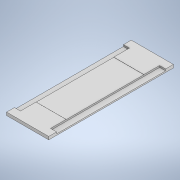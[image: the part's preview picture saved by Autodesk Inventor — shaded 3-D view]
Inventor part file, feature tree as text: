
AUTODESK INVENTOR PART (.ipt)
format: ipt  version: 2020.1 (Build 241239000, 239)  size: 159,744 bytes
history: native  units: mm
features: sketch x6, extrude x5, other x1
ambient origin geometry x8: Origin, YZ Plane, XZ Plane, XY Plane, X Axis, Y Axis, Z Axis, Center Point
bodies: Body1 (feature_tree)
feature tree (12):
  other  "Твердое тело1"
  extrude  "Выдавливание1"  Depth=776.0mm
  extrude  "Выдавливание2"  Depth=280.0mm
  sketch  "Эскиз4"
  extrude  "Выдавливание3"  Depth=20.0mm TaperAngle=0.0deg
  extrude  "Выдавливание4"  Depth=9.0mm
  extrude  "Выдавливание5"  Depth=40.0mm
  sketch  "Эскиз1"
  sketch  "Эскиз3"
  sketch  "Эскиз5"
  sketch  "Эскиз6"
  sketch  "Эскиз7"
